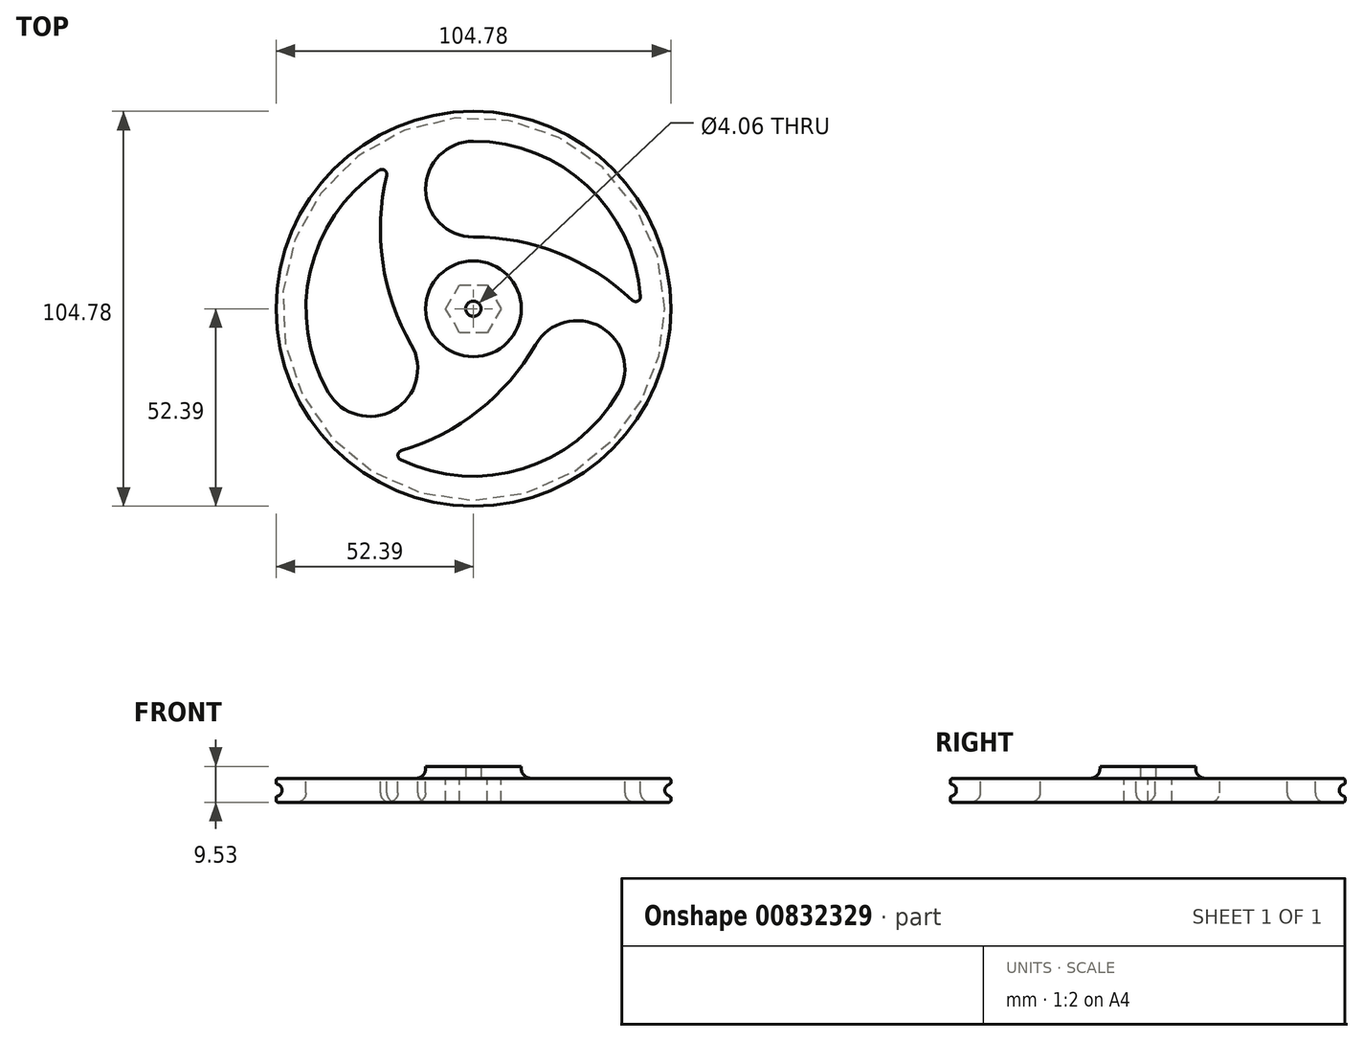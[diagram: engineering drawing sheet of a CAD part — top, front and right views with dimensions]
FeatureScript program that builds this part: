
annotation { "Feature Type Name" : "Feature", "Feature Type Description" : "" }
export const myFeature = defineFeature(function(context is Context, id is Id, definition is map)
    precondition{}
    {
        {
            var Q0;
            Q0=qCreatedBy(makeId("Front.planeOp"),FACE);
            var sketch = newSketch(context, id + "F0", { "sketchPlane" : qUnion([Q0])});
            skLineSegment(sketch, "E0", {"start": v(0, 68.09) * mm, "end": v(0, -70.09) * mm, "construction": true});
            skLineSegment(sketch, "E1", {"start": v(-67.72, 0) * mm, "end": v(64.44, 0) * mm, "construction": true});
            skLineSegment(sketch, "E2", {"start": v(0, 0) * mm, "end": v(0, 3.18) * mm});
            skLineSegment(sketch, "E3", {"start": v(0, 3.17) * mm, "end": v(-52.39, 3.18) * mm});
            skLineSegment(sketch, "E4", {"start": v(-52.39, 3.18) * mm, "end": v(-52.39, 1.59) * mm});
            skArc(sketch, "E5", {"start": v(-52.39, -1.59) * mm, "mid": v(-50.8, 0) * mm, "end": v(-52.39, 1.59) * mm});
            skLineSegment(sketch, "E6", {"start": v(-52.39, 3.18) * mm, "end": v(-52.39, -33.86) * mm, "construction": true});
            skLineSegment(sketch, "E7", {"start": v(-52.39, -1.59) * mm, "end": v(-52.39, -3.18) * mm});
            skLineSegment(sketch, "E8", {"start": v(-52.39, -3.18) * mm, "end": v(0, -3.18) * mm});
            skLineSegment(sketch, "E9", {"start": v(0, 3.18) * mm, "end": v(0, -3.18) * mm});
            skPoint(sketch, "E10", {"position": v(-50.8, 0) * mm});
            skSolve(sketch);
        }
        {
            var Q0;
            Q0 = qSketchRegion(id + "F0", true);
            var Q1;
            Q1=sQuery(id+"F0.wireOp",EDGE,"E0");
            revolve(context, id + "F1", {"surfaceOperationType" : NewSurfaceOperationType.NEW, "entities" : qUnion([Q0]), "axis" : qUnion([Q1]), "revolveType" : RevolveType.FULL});
        }
        {
            var Q0;
            Q0=makeQuery(id+"F1.opRevolve","SWEPT_EDGE",EDGE,{"disambiguationData":[OSD([sQuery(id+"F0.wireOp",EDGE,"E3"),sQuery(id+"F0.wireOp",EDGE,"E4")])]});
            fillet(context, id + "F2", {"entities" : qUnion([Q0]), "radius" : 0.64 * mm, "tangentPropagation" : true, "allowEdgeOverflow" : false});
        }
        {
            var Q0;
            Q0=makeQuery(id+"F1.opRevolve","SWEPT_EDGE",EDGE,{"disambiguationData":[OSD([sQuery(id+"F0.wireOp",EDGE,"E4"),sQuery(id+"F0.wireOp",EDGE,"E5")])]});
            fillet(context, id + "F3", {"entities" : qUnion([Q0]), "radius" : 0.5 * mm, "tangentPropagation" : true, "allowEdgeOverflow" : false});
        }
        {
            var Q0;
            Q0=makeQuery(id+"F1.opRevolve","SWEPT_EDGE",EDGE,{"disambiguationData":[OSD([sQuery(id+"F0.wireOp",EDGE,"E5"),sQuery(id+"F0.wireOp",EDGE,"E7")])]});
            fillet(context, id + "F4", {"entities" : qUnion([Q0]), "radius" : 0.5 * mm, "tangentPropagation" : true, "allowEdgeOverflow" : false});
        }
        {
            var Q0;
            Q0=makeQuery(id+"F1.opRevolve","SWEPT_EDGE",EDGE,{"disambiguationData":[OSD([sQuery(id+"F0.wireOp",EDGE,"E7"),sQuery(id+"F0.wireOp",EDGE,"E8")])]});
            fillet(context, id + "F5", {"entities" : qUnion([Q0]), "radius" : 0.5 * mm, "tangentPropagation" : true, "allowEdgeOverflow" : false});
        }
        {
            var Q0;
            Q0=makeQuery(id+"F1.opRevolve","SWEPT_FACE",FACE,{"disambiguationData":[OSD([sQuery(id+"F0.wireOp",EDGE,"E3")])]});
            var sketch = newSketch(context, id + "F6", { "sketchPlane" : qUnion([Q0])});
            skCircle(sketch, "E11.cCircle", {"center": v(0, 0) * mm, "radius": 6.35 * mm, "construction": true});
            skLineSegment(sketch, "E11.0", {"start": v(3.67, -6.35) * mm, "end": v(-3.67, -6.35) * mm});
            skLineSegment(sketch, "E11.1", {"start": v(-3.67, -6.35) * mm, "end": v(-7.33, 0) * mm});
            skLineSegment(sketch, "E11.2", {"start": v(-7.33, 0) * mm, "end": v(-3.67, 6.35) * mm});
            skLineSegment(sketch, "E11.3", {"start": v(-3.67, 6.35) * mm, "end": v(3.67, 6.35) * mm});
            skLineSegment(sketch, "E11.4", {"start": v(3.67, 6.35) * mm, "end": v(7.33, 0) * mm});
            skLineSegment(sketch, "E11.5", {"start": v(7.33, 0) * mm, "end": v(3.67, -6.35) * mm});
            skPoint(sketch, "E11.0.midPoint", {"position": v(0, -6.35) * mm});
            skLineSegment(sketch, "E12", {"start": v(0, 0) * mm, "end": v(0, 36.93) * mm, "construction": true});
            skLineSegment(sketch, "E13", {"start": v(0, 0) * mm, "end": v(30.24, 0) * mm, "construction": true});
            skSolve(sketch);
        }
        {
            var Q0;
            Q0 = qSketchRegion(id + "F6", true);
            extrude(context, id + "F7", {"entities" : qUnion([Q0]), "operationType" : NewBodyOperationType.REMOVE, "endBound" : BoundingType.UP_TO_NEXT, "oppositeDirection" : true, "depth" : 25.4 * mm, "offsetDistance" : 25.4 * mm});
        }
        {
            var Q0;
            Q0=makeQuery(id+"F1.opRevolve","SWEPT_FACE",FACE,{"disambiguationData":[OSD([sQuery(id+"F0.wireOp",EDGE,"E3")])]});
            var sketch = newSketch(context, id + "F8", { "sketchPlane" : qUnion([Q0])});
            skCircle(sketch, "E14", {"center": v(0, 0) * mm, "radius": 12.7 * mm});
            skCircle(sketch, "E15", {"center": v(0, 0) * mm, "radius": 2.03 * mm});
            skSolve(sketch);
        }
        {
            var Q0;
            Q0 = qSketchRegion(id + "F8", true);
            extrude(context, id + "F9", {"entities" : qUnion([Q0]), "operationType" : NewBodyOperationType.ADD, "depth" : 3.17 * mm, "offsetDistance" : 25.4 * mm});
        }
        {
            var Q0;
            Q0=makeQuery(id+"F1.opRevolve","SWEPT_FACE",FACE,{"disambiguationData":[OSD([sQuery(id+"F0.wireOp",EDGE,"E3")])]});
            var Q1;
            Q1=makeQuery(id+"F9.opExtrude","CAP_EDGE",EDGE,{"disambiguationData":[OSD([sQuery(id+"F8.wireOp",EDGE,"E14")])],"isStart":true});
            fillet(context, id + "F10", {"entities" : qUnion([Q0, Q1]), "radius" : 2.54 * mm, "tangentPropagation" : true, "allowEdgeOverflow" : false});
        }
        {
            var Q0;
            Q0=makeQuery(id+"F1.opRevolve","SWEPT_FACE",FACE,{"disambiguationData":[OSD([sQuery(id+"F0.wireOp",EDGE,"E3")])]});
            var sketch = newSketch(context, id + "F11", { "sketchPlane" : qUnion([Q0])});
            skLineSegment(sketch, "E16", {"start": v(0, 0) * mm, "end": v(85.64, 0) * mm, "construction": true});
            skLineSegment(sketch, "E17", {"start": v(85.64, 0) * mm, "end": v(-56.11, 0) * mm, "construction": true});
            skLineSegment(sketch, "E18", {"start": v(0, 0) * mm, "end": v(63.55, 36.7) * mm, "construction": true});
            skLineSegment(sketch, "E19", {"start": v(63.55, 36.7) * mm, "end": v(-57.49, -33.2) * mm, "construction": true});
            skLineSegment(sketch, "E20", {"start": v(0, 0) * mm, "end": v(0, 49.32) * mm, "construction": true});
            skLineSegment(sketch, "E21", {"start": v(0, 49.32) * mm, "end": v(0, -48.87) * mm, "construction": true});
            skLineSegment(sketch, "E22", {"start": v(0, 0) * mm, "end": v(-49.84, 28.78) * mm, "construction": true});
            skLineSegment(sketch, "E23", {"start": v(-49.84, 28.78) * mm, "end": v(53.92, -31.13) * mm});
            skLineSegment(sketch, "E24", {"start": v(0, 0) * mm, "end": v(26.3, 45.55) * mm, "construction": true});
            skLineSegment(sketch, "E25", {"start": v(26.3, 45.55) * mm, "end": v(-28.32, -49.05) * mm, "construction": true});
            skLineSegment(sketch, "E26", {"start": v(0, 0) * mm, "end": v(-26.71, 46.26) * mm, "construction": true});
            skLineSegment(sketch, "E27", {"start": v(-26.71, 46.26) * mm, "end": v(26.86, -46.52) * mm, "construction": true});
            skArc(sketch, "E28", {"start": v(-25, 36.76) * mm, "mid": v(-43.33, 9.92) * mm, "end": v(-38.5, -22.23) * mm});
            skArc(sketch, "E29", {"start": v(0, 44.45) * mm, "mid": v(-12.7, 31.75) * mm, "end": v(0, 19.05) * mm});
            skArc(sketch, "E30", {"start": v(38.5, -22.22) * mm, "mid": v(33.85, -4.88) * mm, "end": v(16.5, -9.53) * mm});
            skArc(sketch, "E31", {"start": v(-38.5, -22.23) * mm, "mid": v(-21.15, -26.87) * mm, "end": v(-16.5, -9.53) * mm});
            skArc(sketch, "E32", {"start": v(42.2, 2.25) * mm, "mid": v(22.7, 14.7) * mm, "end": v(0, 19.05) * mm});
            skArc(sketch, "E33", {"start": v(-19.14, -37.66) * mm, "mid": v(1.37, -27.01) * mm, "end": v(16.5, -9.53) * mm});
            skArc(sketch, "E34", {"start": v(-23.05, 35.41) * mm, "mid": v(-24.08, 12.32) * mm, "end": v(-16.5, -9.53) * mm});
            skArc(sketch, "E35.trimOffspring", {"start": v(44.33, 3.27) * mm, "mid": v(30.25, 32.57) * mm, "end": v(0, 44.45) * mm});
            skArc(sketch, "E36.trimOffspring", {"start": v(-19.33, -40.02) * mm, "mid": v(13.08, -42.48) * mm, "end": v(38.5, -22.22) * mm});
            skPoint(sketch, "E37.visualSharp", {"position": v(-22.23, 38.5) * mm});
            skArc(sketch, "E37.filletArc", {"start": v(-23.05, 35.41) * mm, "mid": v(-23.56, 36.75) * mm, "end": v(-25, 36.76) * mm});
            skPoint(sketch, "E38.visualSharp", {"position": v(44.45, 0) * mm});
            skArc(sketch, "E38.filletArc", {"start": v(42.2, 2.25) * mm, "mid": v(43.6, 2.03) * mm, "end": v(44.33, 3.27) * mm});
            skPoint(sketch, "E39.visualSharp", {"position": v(-22.22, -38.5) * mm});
            skArc(sketch, "E39.filletArc", {"start": v(-19.14, -37.66) * mm, "mid": v(-20.05, -38.78) * mm, "end": v(-19.33, -40.02) * mm});
            skCircle(sketch, "E40", {"center": v(0, 0) * mm, "radius": 19.05 * mm, "construction": true});
            skSolve(sketch);
        }
        {
            var Q0;
            Q0 = qSketchRegion(id + "F11", true);
            extrude(context, id + "F12", {"entities" : qUnion([Q0]), "operationType" : NewBodyOperationType.REMOVE, "endBound" : BoundingType.THROUGH_ALL, "oppositeDirection" : true, "depth" : 25.4 * mm, "offsetDistance" : 25.4 * mm});
        }
        {
            var Q0;
            Q0=makeQuery(id+"F12.boolean.opBoolean","COPY",EDGE,{"derivedFrom":makeQuery(id+"F12.opExtrude","CAP_EDGE",EDGE,{"disambiguationData":[OSD([sQuery(id+"F11.wireOp",EDGE,"E28")])],"isStart":true})});
            var Q1;
            Q1=makeQuery(id+"F12.boolean.opBoolean","COPY",EDGE,{"derivedFrom":makeQuery(id+"F12.opExtrude","CAP_EDGE",EDGE,{"disambiguationData":[OSD([sQuery(id+"F11.wireOp",EDGE,"E29")])],"isStart":true})});
            var Q2;
            Q2=makeQuery(id+"F12.boolean.opBoolean","COPY",EDGE,{"derivedFrom":makeQuery(id+"F12.opExtrude","CAP_EDGE",EDGE,{"disambiguationData":[OSD([sQuery(id+"F11.wireOp",EDGE,"E30")])],"isStart":true})});
            var Q3;
            Q3=makeQuery(id+"F12.boolean.opBoolean","INTERSECT",EDGE,{"derivedFrom":[makeQuery(id+"F1.opRevolve","SWEPT_FACE",FACE,{"disambiguationData":[OSD([sQuery(id+"F0.wireOp",EDGE,"E8")])]}),makeQuery(id+"F12.opExtrude","SWEPT_FACE",FACE,{"disambiguationData":[OSD([sQuery(id+"F11.wireOp",EDGE,"E30")])]})]});
            var Q4;
            Q4=makeQuery(id+"F12.boolean.opBoolean","INTERSECT",EDGE,{"derivedFrom":[makeQuery(id+"F1.opRevolve","SWEPT_FACE",FACE,{"disambiguationData":[OSD([sQuery(id+"F0.wireOp",EDGE,"E8")])]}),makeQuery(id+"F12.opExtrude","SWEPT_FACE",FACE,{"disambiguationData":[OSD([sQuery(id+"F11.wireOp",EDGE,"E29")])]})]});
            var Q5;
            Q5=makeQuery(id+"F12.boolean.opBoolean","INTERSECT",EDGE,{"derivedFrom":[makeQuery(id+"F1.opRevolve","SWEPT_FACE",FACE,{"disambiguationData":[OSD([sQuery(id+"F0.wireOp",EDGE,"E8")])]}),makeQuery(id+"F12.opExtrude","SWEPT_FACE",FACE,{"disambiguationData":[OSD([sQuery(id+"F11.wireOp",EDGE,"E31")])]})]});
            fillet(context, id + "F13", {"entities" : qUnion([Q0, Q1, Q2, Q3, Q4, Q5]), "radius" : 2.54 * mm, "tangentPropagation" : true, "allowEdgeOverflow" : false});
        }
    });
